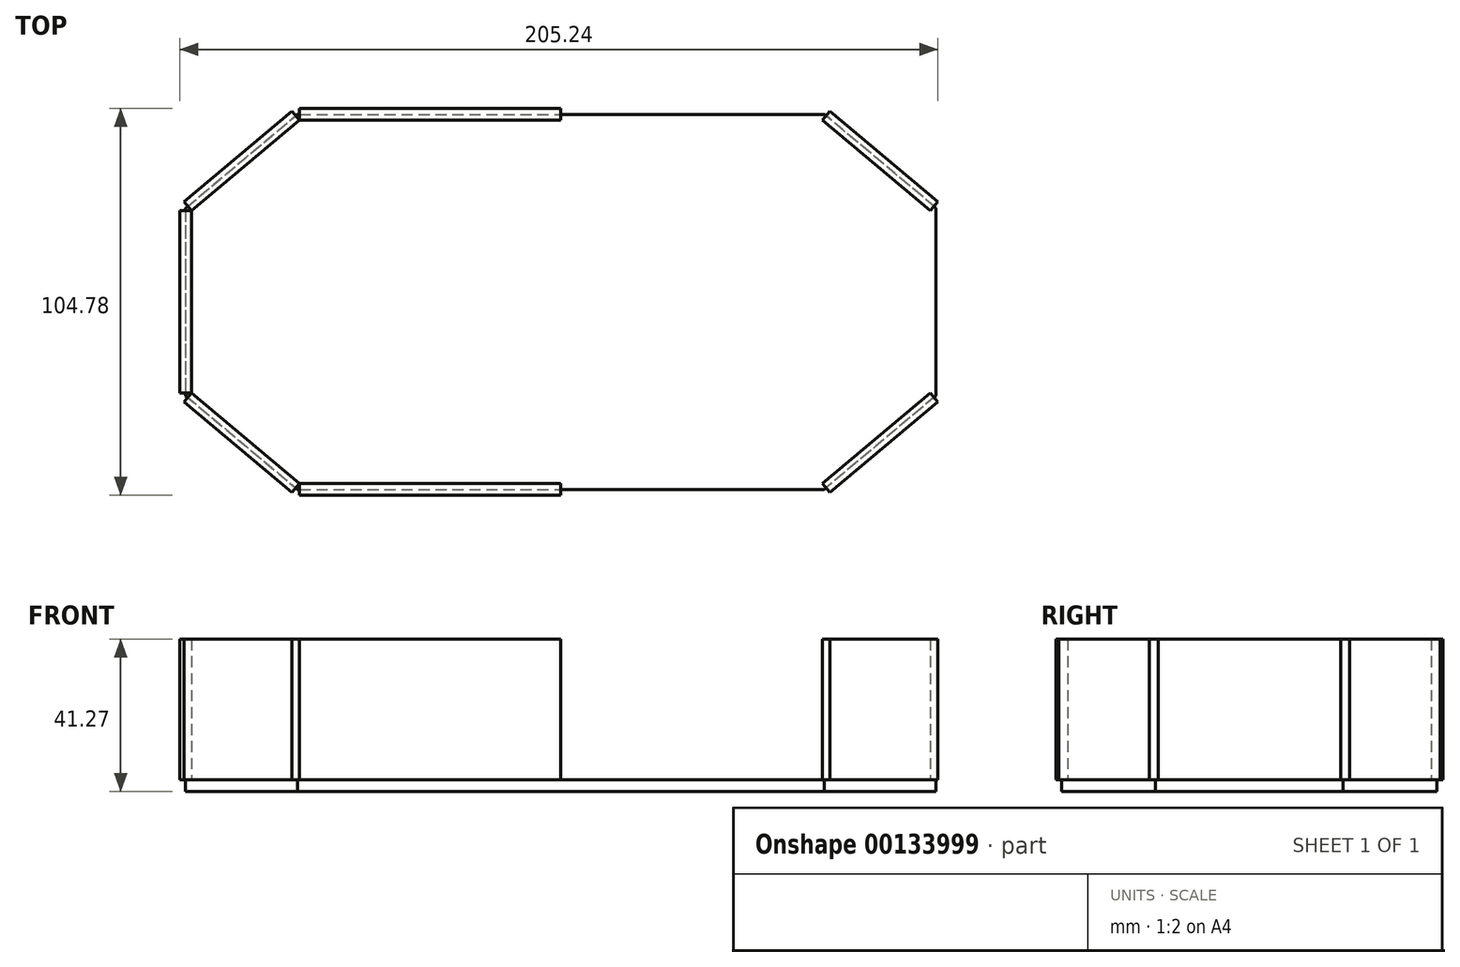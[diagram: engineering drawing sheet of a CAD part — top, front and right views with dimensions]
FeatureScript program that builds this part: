
annotation { "Feature Type Name" : "Feature", "Feature Type Description" : "" }
export const myFeature = defineFeature(function(context is Context, id is Id, definition is map)
    precondition{}
    {
        {
            var Q0;
            Q0=qCreatedBy(makeId("Top.planeOp"),FACE);
            var sketch = newSketch(context, id + "F0", { "sketchPlane" : qUnion([Q0])});
            skLineSegment(sketch, "E0.bottom", {"start": v(-20.53, 50.8) * mm, "end": v(50.8, 50.8) * mm});
            skLineSegment(sketch, "E0.top", {"start": v(-20.53, -50.8) * mm, "end": v(50.8, -50.8) * mm});
            skLineSegment(sketch, "E0.left", {"start": v(-50.8, 25.4) * mm, "end": v(-50.8, -25.4) * mm});
            skLineSegment(sketch, "E0.right", {"start": v(50.8, 50.8) * mm, "end": v(50.8, -50.8) * mm});
            skPoint(sketch, "E0.middle", {"position": v(0, 0) * mm});
            skLineSegment(sketch, "E1", {"start": v(-50.8, 25.4) * mm, "end": v(-20.53, 50.8) * mm});
            skLineSegment(sketch, "E2", {"start": v(-50.8, -25.4) * mm, "end": v(-20.53, -50.8) * mm});
            skLineSegment(sketch, "E3", {"start": v(-20.53, 50.8) * mm, "end": v(-20.53, -50.8) * mm, "construction": true});
            skPoint(sketch, "E4.orphan", {"position": v(-50.8, 50.8) * mm});
            skPoint(sketch, "E5.orphan", {"position": v(-50.8, -50.8) * mm});
            skSolve(sketch);
        }
        {
            var Q0;
            Q0 = qSketchRegion(id + "F0", true);
            extrude(context, id + "F1", {"entities" : qUnion([Q0]), "depth" : 3.17 * mm});
        }
        {
            var Q0;
            Q0=makeQuery(id+"F1.opExtrude","CAP_FACE",FACE,{"disambiguationData":[OSD([sQuery(id+"F0.wireOp",EDGE,"E0.bottom"),sQuery(id+"F0.wireOp",EDGE,"E0.top"),sQuery(id+"F0.wireOp",EDGE,"E0.left"),sQuery(id+"F0.wireOp",EDGE,"E0.right"),sQuery(id+"F0.wireOp",EDGE,"E1"),sQuery(id+"F0.wireOp",EDGE,"E2")])],"isStart":false});
            var sketch = newSketch(context, id + "F2", { "sketchPlane" : qUnion([Q0])});
            skLineSegment(sketch, "E6.1", {"start": v(-19.95, 49.21) * mm, "end": v(-49.21, 24.66) * mm});
            skLineSegment(sketch, "E6.2", {"start": v(-49.21, 24.66) * mm, "end": v(-49.21, -24.66) * mm});
            skLineSegment(sketch, "E6.3", {"start": v(50.8, 49.21) * mm, "end": v(-19.95, 49.21) * mm});
            skLineSegment(sketch, "E6.4", {"start": v(-49.21, -24.66) * mm, "end": v(-19.95, -49.21) * mm});
            skLineSegment(sketch, "E6.5", {"start": v(-19.95, -49.21) * mm, "end": v(50.8, -49.21) * mm});
            skLineSegment(sketch, "E7.1", {"start": v(-22, 51.64) * mm, "end": v(-51.25, 27.1) * mm});
            skLineSegment(sketch, "E7.2", {"start": v(-52.39, 24.66) * mm, "end": v(-52.39, -24.66) * mm});
            skLineSegment(sketch, "E7.3", {"start": v(50.8, 52.39) * mm, "end": v(-19.95, 52.39) * mm});
            skLineSegment(sketch, "E7.4", {"start": v(-51.25, -27.1) * mm, "end": v(-22, -51.64) * mm});
            skLineSegment(sketch, "E7.5", {"start": v(-19.95, -52.39) * mm, "end": v(50.8, -52.39) * mm});
            skLineSegment(sketch, "E8.0", {"start": v(50.8, 52.39) * mm, "end": v(50.8, 49.21) * mm});
            skPoint(sketch, "E9.orphan", {"position": v(50.8, -50.8) * mm});
            skPoint(sketch, "E10.orphan", {"position": v(50.8, 50.8) * mm});
            skLineSegment(sketch, "E11.trimOffspring", {"start": v(50.8, -49.21) * mm, "end": v(50.8, -52.39) * mm});
            skLineSegment(sketch, "E12", {"start": v(-49.21, -24.66) * mm, "end": v(-52.39, -24.66) * mm});
            skLineSegment(sketch, "E13", {"start": v(-49.21, 24.66) * mm, "end": v(-52.39, 24.66) * mm});
            skLineSegment(sketch, "E14", {"start": v(-49.21, 24.66) * mm, "end": v(-51.25, 27.1) * mm});
            skLineSegment(sketch, "E15", {"start": v(-19.95, 49.21) * mm, "end": v(-22, 51.64) * mm});
            skLineSegment(sketch, "E16", {"start": v(-19.95, 49.21) * mm, "end": v(-19.95, 52.39) * mm});
            skLineSegment(sketch, "E17", {"start": v(-49.21, -24.66) * mm, "end": v(-51.25, -27.1) * mm});
            skLineSegment(sketch, "E18", {"start": v(-19.95, -49.21) * mm, "end": v(-22, -51.64) * mm});
            skLineSegment(sketch, "E19", {"start": v(-19.95, -49.21) * mm, "end": v(-19.95, -52.39) * mm});
            skSolve(sketch);
        }
        {
            var Q0;
            {var subQ0=sQuery(id+"F2.wireOp",EDGE,"E6.4");Q0=makeQuery(id+"F2.imprint","IMPRINT",FACE,{"disambiguationData":[TD([[makeQuery(id+"F2.imprint","IMPRINT",EDGE,{"derivedFrom":subQ0}),-1.0]])]});}
            var Q1;
            {var subQ0=sQuery(id+"F2.wireOp",EDGE,"E7.4");Q1=makeQuery(id+"F2.imprint","IMPRINT",FACE,{"disambiguationData":[TD([[makeQuery(id+"F2.imprint","IMPRINT",EDGE,{"derivedFrom":subQ0}),1.0]])]});}
            var Q2;
            {var subQ0=sQuery(id+"F2.wireOp",EDGE,"E7.1");Q2=makeQuery(id+"F2.imprint","IMPRINT",FACE,{"disambiguationData":[TD([[makeQuery(id+"F2.imprint","IMPRINT",EDGE,{"derivedFrom":subQ0}),1.0]])]});}
            var Q3;
            {var subQ0=sQuery(id+"F2.wireOp",EDGE,"E6.1");Q3=makeQuery(id+"F2.imprint","IMPRINT",FACE,{"disambiguationData":[TD([[makeQuery(id+"F2.imprint","IMPRINT",EDGE,{"derivedFrom":subQ0}),-1.0]])]});}
            extrude(context, id + "F3", {"entities" : qUnion([Q0, Q1, Q2, Q3]), "operationType" : NewBodyOperationType.ADD, "depth" : 38.1 * mm});
        }
        {
            var Q0;
            Q0=makeQuery(id+"F1.opExtrude","SWEPT_BODY",BODY,{"disambiguationData":[OSD([sQuery(id+"F0.wireOp",EDGE,"E0.bottom"),sQuery(id+"F0.wireOp",EDGE,"E0.top"),sQuery(id+"F0.wireOp",EDGE,"E0.left"),sQuery(id+"F0.wireOp",EDGE,"E0.right"),sQuery(id+"F0.wireOp",EDGE,"E1"),sQuery(id+"F0.wireOp",EDGE,"E2")])]});
            var Q1;
            Q1=makeQuery(id+"F1.opExtrude","SWEPT_FACE",FACE,{"disambiguationData":[OSD([sQuery(id+"F0.wireOp",EDGE,"E0.right")])]});
            mirror(context, id + "F4", {"operationType" : NewBodyOperationType.ADD, "entities" : qUnion([Q0]), "mirrorPlane" : qUnion([Q1])});
        }
        {
            var Q0;
            {var subQ0=sQuery(id+"F2.wireOp",EDGE,"E6.2");Q0=makeQuery(id+"F2.imprint","IMPRINT",FACE,{"disambiguationData":[TD([[makeQuery(id+"F2.imprint","IMPRINT",EDGE,{"derivedFrom":subQ0}),-1.0]])]});}
            var Q1;
            {var subQ0=sQuery(id+"F2.wireOp",EDGE,"E7.2");Q1=makeQuery(id+"F2.imprint","IMPRINT",FACE,{"disambiguationData":[TD([[makeQuery(id+"F2.imprint","IMPRINT",EDGE,{"derivedFrom":subQ0}),1.0]])]});}
            var Q2;
            {var subQ0=sQuery(id+"F2.wireOp",EDGE,"E7.3");Q2=makeQuery(id+"F2.imprint","IMPRINT",FACE,{"disambiguationData":[TD([[makeQuery(id+"F2.imprint","IMPRINT",EDGE,{"derivedFrom":subQ0}),1.0]])]});}
            var Q3;
            {var subQ0=sQuery(id+"F2.wireOp",EDGE,"E6.3");Q3=makeQuery(id+"F2.imprint","IMPRINT",FACE,{"disambiguationData":[TD([[makeQuery(id+"F2.imprint","IMPRINT",EDGE,{"derivedFrom":subQ0}),-1.0]])]});}
            var Q4;
            {var subQ0=sQuery(id+"F2.wireOp",EDGE,"E6.5");Q4=makeQuery(id+"F2.imprint","IMPRINT",FACE,{"disambiguationData":[TD([[makeQuery(id+"F2.imprint","IMPRINT",EDGE,{"derivedFrom":subQ0}),-1.0]])]});}
            var Q5;
            {var subQ0=sQuery(id+"F2.wireOp",EDGE,"E7.5");Q5=makeQuery(id+"F2.imprint","IMPRINT",FACE,{"disambiguationData":[TD([[makeQuery(id+"F2.imprint","IMPRINT",EDGE,{"derivedFrom":subQ0}),1.0]])]});}
            extrude(context, id + "F5", {"entities" : qUnion([Q0, Q1, Q2, Q3, Q4, Q5]), "depth" : 38.1 * mm});
        }
    });
